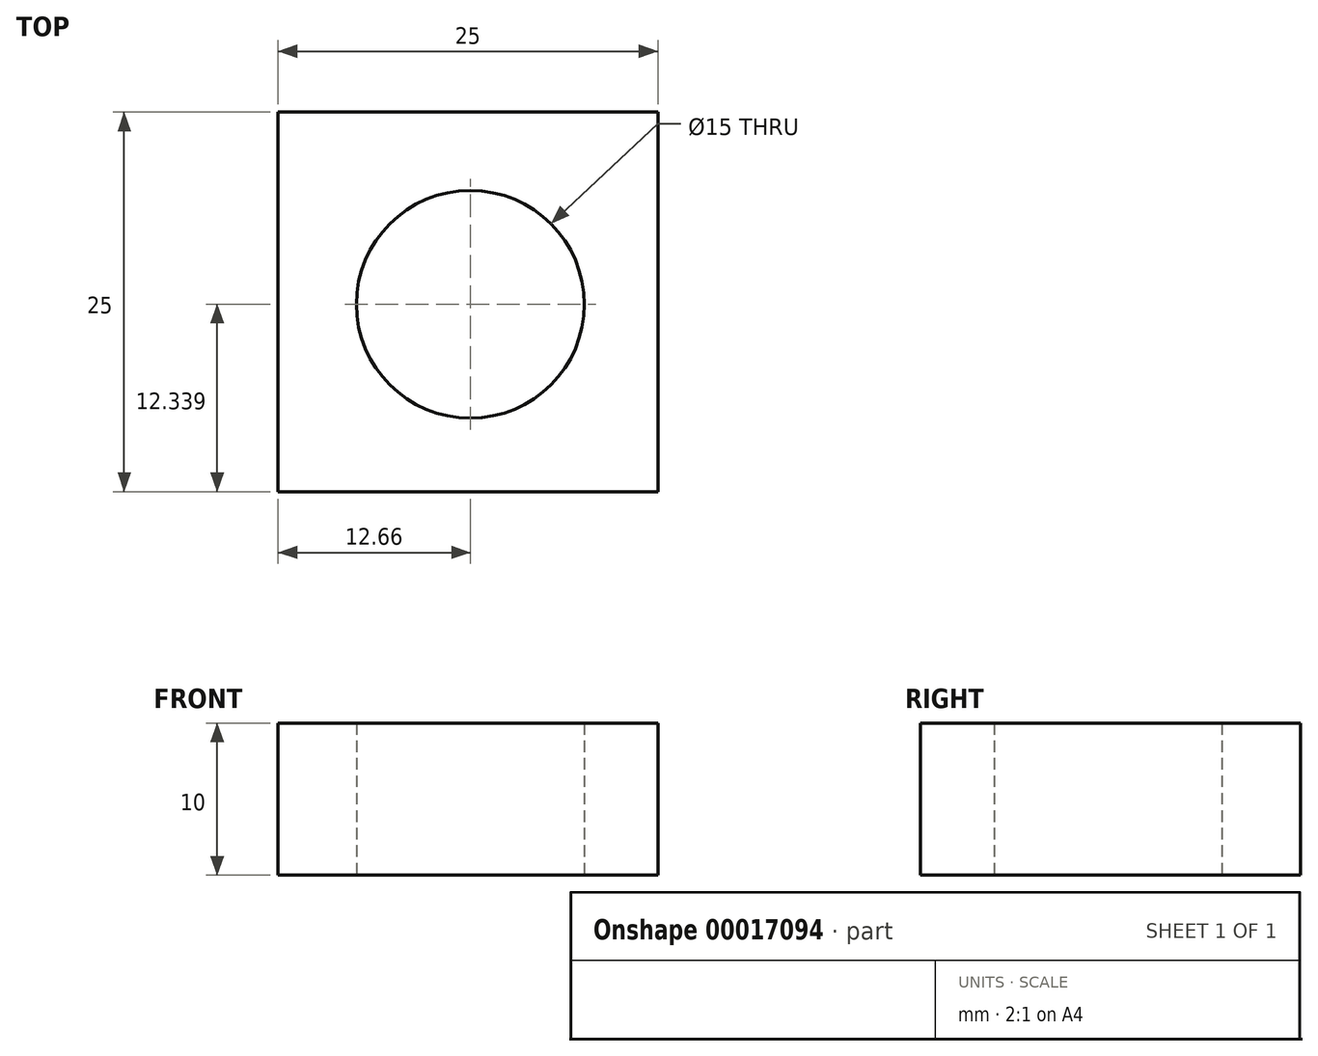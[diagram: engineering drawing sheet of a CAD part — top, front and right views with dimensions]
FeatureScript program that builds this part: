
annotation { "Feature Type Name" : "Feature", "Feature Type Description" : "" }
export const myFeature = defineFeature(function(context is Context, id is Id, definition is map)
    precondition{}
    {
        {
            var Q0;
            Q0=qCreatedBy(makeId("Top.planeOp"),FACE);
            var sketch = newSketch(context, id + "F0", { "sketchPlane" : qUnion([Q0])});
            skLineSegment(sketch, "E0.bottom", {"start": v(-12.66, 10.67) * mm, "end": v(12.34, 10.67) * mm});
            skLineSegment(sketch, "E0.top", {"start": v(-12.66, -14.33) * mm, "end": v(12.34, -14.33) * mm});
            skLineSegment(sketch, "E0.left", {"start": v(-12.66, 10.67) * mm, "end": v(-12.66, -14.33) * mm});
            skLineSegment(sketch, "E0.right", {"start": v(12.34, 10.67) * mm, "end": v(12.34, -14.33) * mm});
            skCircle(sketch, "E1", {"center": v(0, -2) * mm, "radius": 7.5 * mm});
            skSolve(sketch);
        }
        {
            var Q0;
            Q0=makeQuery(id+"F0.imprint","IMPRINT",FACE,{"disambiguationData":[TD([[makeQuery(id+"F0.imprint","IMPRINT",EDGE,{"derivedFrom":sQuery(id+"F0.wireOp",EDGE,"E0.bottom")}),-1.0]])]});
            extrude(context, id + "F1", {"entities" : qUnion([Q0]), "depth" : 10 * mm});
        }
    });
